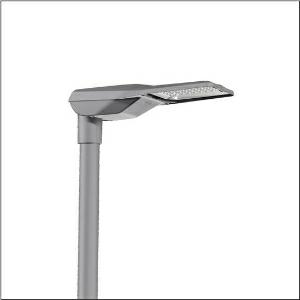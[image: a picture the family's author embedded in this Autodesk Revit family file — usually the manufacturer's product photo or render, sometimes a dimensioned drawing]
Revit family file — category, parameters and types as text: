
# Revit family: streetlight_sl_21_iq_mini___st0_8a_5xe2c41g08jb_e7d2
name_source: partatom
category: Lighting Fixtures
units: mm (PartAtom-declared; Revit-internal decimal feet)

## family parameters
Cut with Voids When Loaded = No
Host = Face
Light Source = No
Part Type = Normal
Room Calculation Point = No
Round Connector Dimension = Use Diameter
Shared = No

## types (1)
- --- (1 x LED, 11290 lm, 71.6 W, 4000K)
    Apparent Load = 72 VA
    CIE Flux Codes = 41 75 97 100 100
    Color Rendering = 70
    Color Temperature = 4000K
    Default Elevation = 1800 mm
    Description = Streetlight SL 21 iQ mini, mast luminaire, primary light control with lens, of PMMA, primary optical cover: cover, of toughened safety glass, transparent, light distribution: ST0.8a, light emission: direct distribution, primary light characteristic: asymmetric, installation type: post-top, side-entry, LED, High Power LED, rated luminous flux: 11.290lm, luminous efficacy: 158lm/W, light colour: 740, colour temperature: 4000K, control gear: iQ Street-Remote, control: Street-Remote, Auto-Match, Temp-Guard, Lumen-Switch, Night-Set, Smart-Wire, Light-Fading, Desk-Remote (wireless, voltage-free reading and setting of iQ features in the workshop via application-optimized NFC function/RFID function), optimised constant luminous flux control (CLO 2.0), pre-setting: linear dimming characteristic, mains connection: 220..240V, AC, 50/60Hz, start of lifetime: 72W, end of service life: 75W, reduction: 33W, luminaire housing, of diecast aluminium, powder-coated, Siteco® metallic grey (DB 702S), corrosivity category C5 mid according to DIN EN ISO 12944, please order mast flange separately, inclination adjustable: 0°, 5°, 10°, 15°, sealing non-destructively replaceable, multi-level sealing system, length: 628mm, width: 235mm, height: 110mm, mast flange for spigot size: 42mm (side-entry): 5XC10008XM4, 60/48mm (side-entry/post-top): 5XC10108XM2, 76/60mm (side-entry/post-top): 5XC10108XM1, mounting height: 4..8m, protection rating (complete): IP66, insulation class (complete): insulation class II (safety insulation), certification: CE, ENEC, ENEC+, VDE, impact resistance: IK10, permissible operating ambient temperature for outdoor applications: -40..+50°C, standard-compliant lighting for roads and squares, packaging unit: 1 piece

Light Distribution: ST0.8a
    Height = 110 mm
    Lamp = 1 x LED
    Lamp Light Flux = 11290 lm
    Lamp Power = 71.6 W
    Lamp count = 1
    Length = 625 mm
    Luminous efficacy = 158 lm/W
    Manufacturer = Siteco
    ModVariant = No
    Model = 5XE2C41G08JB
    Number of Poles = 1
    OnlyDefault = Yes
    Power Factor = 1
    Product Name = Streetlight SL 21 iQ mini | ST0.8a
    Product group = mast luminaire | pylon top
    ProductGroupID = 6100
    Protection Class = Protection class II
    Protection Degree = IP 66
    RLX_Detail_Level = 1
    RLX_Emergency_Light_Flux = 0 lm
    RLX_Emergency_Type = 0
    RLX_Emergency_Type_DB = No
    RlxData = <blob elided: 26341 chars, md5=387d1740>
    Socket = socket
    Standby Power = 0 W
    System Light Flux = 11290 lm
    System Power = 72 W
    Type Comments = factory setting: luminous flux: 100 % | dim-lin: 254 | 746 mA
    Type Image = l_1003519.jpg
    URL = http://relux.com
    VarID = @adj_169192
    Voltage = 0 V
    Weight = 0.00 kg
    Width = 234 mm

## geometry (parser evidence)
native form markers: Blend x4, Sweep x10
no freeform markers — native parametric forms only
